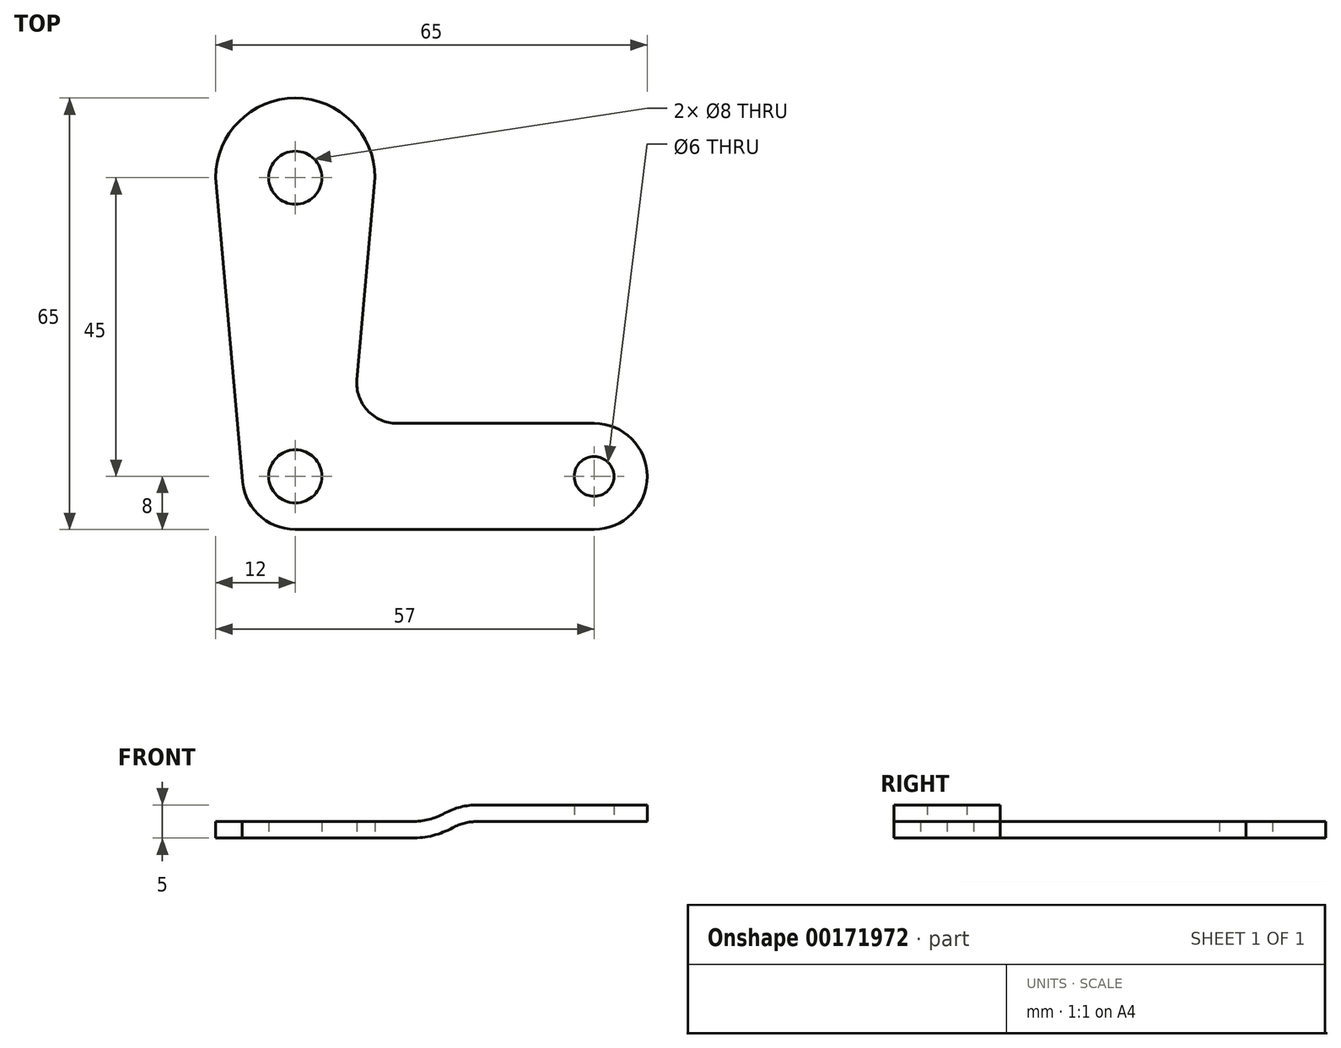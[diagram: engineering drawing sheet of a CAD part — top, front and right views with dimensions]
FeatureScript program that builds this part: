
annotation { "Feature Type Name" : "Feature", "Feature Type Description" : "" }
export const myFeature = defineFeature(function(context is Context, id is Id, definition is map)
    precondition{}
    {
        {
            var Q0;
            Q0=qCreatedBy(makeId("Top.planeOp"),FACE);
            var sketch = newSketch(context, id + "F0", { "sketchPlane" : qUnion([Q0])});
            skCircle(sketch, "E0", {"center": v(0, 0) * mm, "radius": 4 * mm});
            skCircle(sketch, "E1", {"center": v(45, 0) * mm, "radius": 3 * mm});
            skCircle(sketch, "E2", {"center": v(0, 45) * mm, "radius": 4 * mm});
            skArc(sketch, "E3", {"start": v(45, 8) * mm, "mid": v(53, 0) * mm, "end": v(45, -8) * mm});
            skArc(sketch, "E4", {"start": v(-12, 45) * mm, "mid": v(0, 57) * mm, "end": v(12, 45) * mm});
            skArc(sketch, "E5", {"start": v(-8, 0) * mm, "mid": v(-5.66, -5.66) * mm, "end": v(0, -8) * mm});
            skLineSegment(sketch, "E6", {"start": v(-12, 45) * mm, "end": v(-8, 0) * mm});
            skLineSegment(sketch, "E7", {"start": v(0, -8) * mm, "end": v(45, -8) * mm});
            skLineSegment(sketch, "E8", {"start": v(0, 60.68) * mm, "end": v(0, -23.04) * mm, "construction": true});
            skLineSegment(sketch, "E9.MirrorCS", {"start": v(12, 45) * mm, "end": v(9.3, 14.53) * mm});
            skLineSegment(sketch, "E10", {"start": v(45, 8) * mm, "end": v(15.27, 8) * mm});
            skPoint(sketch, "E11.orphan", {"position": v(8, 0) * mm});
            skPoint(sketch, "E12.visualSharp", {"position": v(8.71, 8) * mm});
            skArc(sketch, "E12.filletArc", {"start": v(9.3, 14.53) * mm, "mid": v(10.84, 9.95) * mm, "end": v(15.27, 8) * mm});
            skSolve(sketch);
        }
        {
            var Q0;
            Q0=makeQuery(id+"F0.imprint","IMPRINT",FACE,{"disambiguationData":[TD([[makeQuery(id+"F0.imprint","IMPRINT",EDGE,{"derivedFrom":sQuery(id+"F0.wireOp",EDGE,"E0")}),-1.0]])]});
            extrude(context, id + "F1", {"entities" : qUnion([Q0]), "endBound" : BoundingType.SYMMETRIC, "depth" : 5 * mm});
        }
        {
            var Q0;
            Q0=makeQuery(id+"F1.opExtrude","SWEPT_FACE",FACE,{"disambiguationData":[OSD([sQuery(id+"F0.wireOp",EDGE,"E7")])]});
            var sketch = newSketch(context, id + "F2", { "sketchPlane" : qUnion([Q0])});
            skLineSegment(sketch, "E13.bottom", {"start": v(-12, -2.5) * mm, "end": v(22.5, -2.5) * mm});
            skLineSegment(sketch, "E13.top", {"start": v(-12, 0) * mm, "end": v(22.5, 0) * mm});
            skLineSegment(sketch, "E13.left", {"start": v(-12, -2.5) * mm, "end": v(-12, 0) * mm});
            skLineSegment(sketch, "E13.right", {"start": v(22.5, -2.5) * mm, "end": v(22.5, 0) * mm});
            skLineSegment(sketch, "E14.bottom", {"start": v(22.5, 0) * mm, "end": v(53, 0) * mm});
            skLineSegment(sketch, "E14.top", {"start": v(27.43, 2.5) * mm, "end": v(53, 2.5) * mm});
            skLineSegment(sketch, "E14.left", {"start": v(22.5, 0) * mm, "end": v(22.5, 1.25) * mm});
            skLineSegment(sketch, "E14.right", {"start": v(53, 0) * mm, "end": v(53, 2.5) * mm});
            skArc(sketch, "E15", {"start": v(27.43, 2.5) * mm, "mid": v(24.89, 2.18) * mm, "end": v(22.5, 1.25) * mm});
            skArc(sketch, "E16", {"start": v(22.5, 1.25) * mm, "mid": v(20.11, 0.32) * mm, "end": v(17.57, 0) * mm});
            skArc(sketch, "E17.0", {"start": v(23.7, -0.95) * mm, "mid": v(20.73, -2.1) * mm, "end": v(17.57, -2.5) * mm});
            skArc(sketch, "E18.0", {"start": v(27.43, 0) * mm, "mid": v(25.5, -0.24) * mm, "end": v(23.7, -0.95) * mm});
            skLineSegment(sketch, "E19", {"start": v(27.43, 2.5) * mm, "end": v(-12, 2.5) * mm});
            skLineSegment(sketch, "E20", {"start": v(-12, 2.5) * mm, "end": v(-12, 0) * mm});
            skLineSegment(sketch, "E21", {"start": v(-12, 0) * mm, "end": v(17.57, 0) * mm});
            skLineSegment(sketch, "E22", {"start": v(17.57, -2.5) * mm, "end": v(53, -2.5) * mm});
            skLineSegment(sketch, "E23", {"start": v(53, -2.5) * mm, "end": v(53, 0) * mm});
            skSolve(sketch);
        }
        {
            var Q0;
            {var subQ3=sQuery(id+"F2.wireOp",EDGE,"E20");Q0=makeQuery(id+"F2.imprint","IMPRINT",FACE,{"disambiguationData":[TD([[makeQuery(id+"F2.imprint","IMPRINT",EDGE,{"derivedFrom":subQ3}),1.0]])]});}
            var Q1;
            {var subQ6=sQuery(id+"F2.wireOp",EDGE,"E15");Q1=makeQuery(id+"F2.imprint","IMPRINT",FACE,{"disambiguationData":[TD([[makeQuery(id+"F2.imprint","IMPRINT",EDGE,{"derivedFrom":subQ6}),-1.0]])]});}
            var Q2;
            {var subQ0=sQuery(id+"F2.wireOp",EDGE,"E22");var subQ1=sQuery(id+"F2.wireOp",EDGE,"E13.right");var subQ2=makeQuery(id+"F2.imprint","INTERSECT",VERTEX,{"derivedFrom":[subQ1,subQ0]});Q2=makeQuery(id+"F2.imprint","IMPRINT",FACE,{"disambiguationData":[TD([[makeQuery(id+"F2.imprint","IMPRINT",EDGE,{"disambiguationData":[TD([[subQ2,-1.0]])],"derivedFrom":subQ1}),1.0]])]});}
            var Q3;
            {var subQ0=sQuery(id+"F2.wireOp",EDGE,"E18.0");Q3=makeQuery(id+"F2.imprint","IMPRINT",FACE,{"disambiguationData":[TD([[makeQuery(id+"F2.imprint","IMPRINT",EDGE,{"derivedFrom":subQ0}),1.0]])]});}
            var Q4;
            {var subQ0=sQuery(id+"F2.wireOp",EDGE,"E23");Q4=makeQuery(id+"F2.imprint","IMPRINT",FACE,{"disambiguationData":[TD([[makeQuery(id+"F2.imprint","IMPRINT",EDGE,{"derivedFrom":subQ0}),1.0]])]});}
            extrude(context, id + "F3", {"entities" : qUnion([Q0, Q1, Q2, Q3, Q4]), "operationType" : NewBodyOperationType.REMOVE, "endBound" : BoundingType.THROUGH_ALL, "oppositeDirection" : true, "depth" : 25 * mm});
        }
    });
